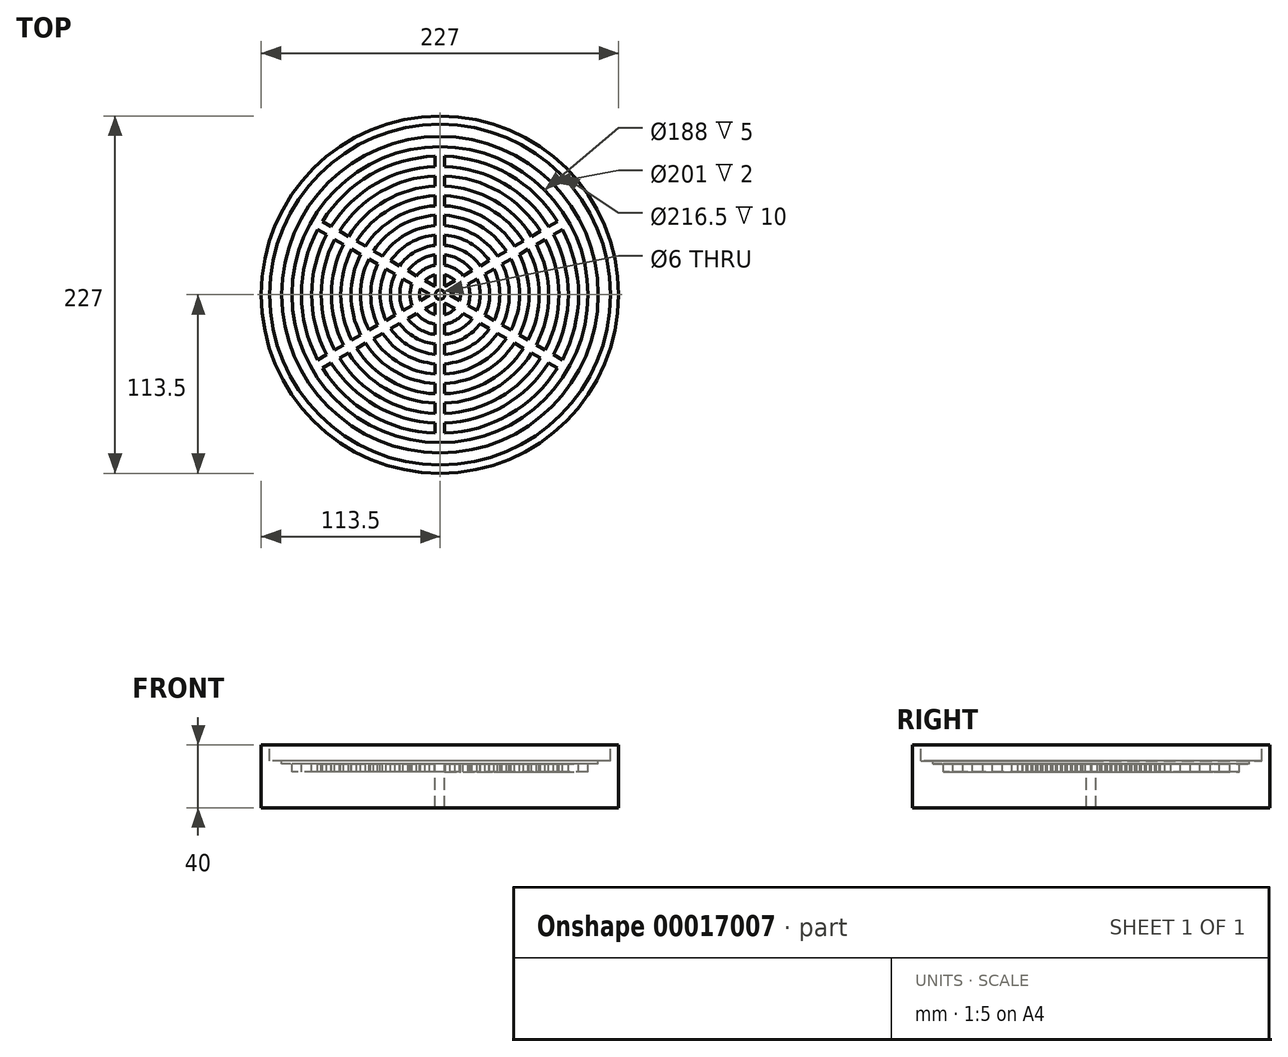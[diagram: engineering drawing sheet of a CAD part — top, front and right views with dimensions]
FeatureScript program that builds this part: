
annotation { "Feature Type Name" : "Feature", "Feature Type Description" : "" }
export const myFeature = defineFeature(function(context is Context, id is Id, definition is map)
    precondition{}
    {
        {
            var Q0;
            Q0=qCreatedBy(makeId("Front.planeOp"),FACE);
            var sketch = newSketch(context, id + "F0", { "sketchPlane" : qUnion([Q0])});
            skLineSegment(sketch, "E0", {"start": v(-113.5, 0) * mm, "end": v(-108.25, 0) * mm});
            skLineSegment(sketch, "E1", {"start": v(-108.25, 0) * mm, "end": v(-108.25, -10) * mm});
            skLineSegment(sketch, "E2", {"start": v(-108.25, -10) * mm, "end": v(-100.5, -10) * mm});
            skLineSegment(sketch, "E3", {"start": v(-100.5, -10) * mm, "end": v(-100.5, -12) * mm});
            skLineSegment(sketch, "E4", {"start": v(-3, -17) * mm, "end": v(-3, -40) * mm});
            skLineSegment(sketch, "E5", {"start": v(-3, -40) * mm, "end": v(-113.5, -40) * mm});
            skLineSegment(sketch, "E6", {"start": v(-113.5, -40) * mm, "end": v(-113.5, 0) * mm});
            skLineSegment(sketch, "E7", {"start": v(0, 37.77) * mm, "end": v(0, -35.64) * mm, "construction": true});
            skLineSegment(sketch, "E8", {"start": v(-100.5, -12) * mm, "end": v(-94, -12) * mm});
            skLineSegment(sketch, "E9", {"start": v(-94, -12) * mm, "end": v(-94, -17) * mm});
            skLineSegment(sketch, "E10", {"start": v(-94, -17) * mm, "end": v(-88, -17) * mm});
            skLineSegment(sketch, "E11", {"start": v(-88, -17) * mm, "end": v(-88, -12) * mm});
            skLineSegment(sketch, "E12.1.0.0", {"start": v(-75.5, -17) * mm, "end": v(-75.5, -12) * mm});
            skLineSegment(sketch, "E12.1.0.1", {"start": v(-81.5, -17) * mm, "end": v(-75.5, -17) * mm});
            skLineSegment(sketch, "E12.1.0.2", {"start": v(-81.5, -12) * mm, "end": v(-81.5, -17) * mm});
            skLineSegment(sketch, "E12.1.0.3", {"start": v(-88, -12) * mm, "end": v(-81.5, -12) * mm});
            skLineSegment(sketch, "E12.2.0.0", {"start": v(-63, -17) * mm, "end": v(-63, -12) * mm});
            skLineSegment(sketch, "E12.2.0.1", {"start": v(-69, -17) * mm, "end": v(-63, -17) * mm});
            skLineSegment(sketch, "E12.2.0.2", {"start": v(-69, -12) * mm, "end": v(-69, -17) * mm});
            skLineSegment(sketch, "E12.2.0.3", {"start": v(-75.5, -12) * mm, "end": v(-69, -12) * mm});
            skLineSegment(sketch, "E12.3.0.0", {"start": v(-50.5, -17) * mm, "end": v(-50.5, -12) * mm});
            skLineSegment(sketch, "E12.3.0.1", {"start": v(-56.5, -17) * mm, "end": v(-50.5, -17) * mm});
            skLineSegment(sketch, "E12.3.0.2", {"start": v(-56.5, -12) * mm, "end": v(-56.5, -17) * mm});
            skLineSegment(sketch, "E12.3.0.3", {"start": v(-63, -12) * mm, "end": v(-56.5, -12) * mm});
            skLineSegment(sketch, "E12.4.0.0", {"start": v(-38, -17) * mm, "end": v(-38, -12) * mm});
            skLineSegment(sketch, "E12.4.0.1", {"start": v(-44, -17) * mm, "end": v(-38, -17) * mm});
            skLineSegment(sketch, "E12.4.0.2", {"start": v(-44, -12) * mm, "end": v(-44, -17) * mm});
            skLineSegment(sketch, "E12.4.0.3", {"start": v(-50.5, -12) * mm, "end": v(-44, -12) * mm});
            skLineSegment(sketch, "E12.5.0.0", {"start": v(-25.5, -17) * mm, "end": v(-25.5, -12) * mm});
            skLineSegment(sketch, "E12.5.0.1", {"start": v(-31.5, -17) * mm, "end": v(-25.5, -17) * mm});
            skLineSegment(sketch, "E12.5.0.2", {"start": v(-31.5, -12) * mm, "end": v(-31.5, -17) * mm});
            skLineSegment(sketch, "E12.5.0.3", {"start": v(-38, -12) * mm, "end": v(-31.5, -12) * mm});
            skLineSegment(sketch, "E12.6.0.0", {"start": v(-13, -17) * mm, "end": v(-13, -12) * mm});
            skLineSegment(sketch, "E12.6.0.1", {"start": v(-19, -17) * mm, "end": v(-13, -17) * mm});
            skLineSegment(sketch, "E12.6.0.2", {"start": v(-19, -12) * mm, "end": v(-19, -17) * mm});
            skLineSegment(sketch, "E12.6.0.3", {"start": v(-25.5, -12) * mm, "end": v(-19, -12) * mm});
            skLineSegment(sketch, "E12.direction1", {"start": v(-88, -17) * mm, "end": v(-75.5, -17) * mm, "construction": true});
            skLineSegment(sketch, "E13.6.7.0", {"start": v(-6.5, -12) * mm, "end": v(-6.5, -17) * mm});
            skLineSegment(sketch, "E13.9.7.0", {"start": v(-13, -12) * mm, "end": v(-6.5, -12) * mm});
            skLineSegment(sketch, "E14", {"start": v(-6.5, -17) * mm, "end": v(-3, -17) * mm});
            skSolve(sketch);
        }
        {
            var Q0;
            Q0=makeQuery(id+"F0.imprint","IMPRINT",FACE,{"disambiguationData":[TD([[makeQuery(id+"F0.imprint","IMPRINT",EDGE,{"derivedFrom":sQuery(id+"F0.wireOp",EDGE,"E0")}),-1.0]])]});
            var Q1;
            Q1=sQuery(id+"F0.wireOp",EDGE,"E7");
            var Q2;
            Q2=sQuery(id+"F0.wireOp",EDGE,"E7");
            revolve(context, id + "F1", {"entities" : qUnion([Q0]), "surfaceEntities" : qUnion([Q1]), "axis" : qUnion([Q2]), "revolveType" : RevolveType.FULL});
        }
        {
            var Q0;
            Q0=qCreatedBy(makeId("Top.planeOp"),FACE);
            var sketch = newSketch(context, id + "F2", { "sketchPlane" : qUnion([Q0])});
            skLineSegment(sketch, "E15.rect.bottom", {"start": v(0, 94) * mm, "end": v(0, 94) * mm});
            skLineSegment(sketch, "E15.rect.top", {"start": v(0, -94) * mm, "end": v(0, -94) * mm});
            skLineSegment(sketch, "E15.rect.left", {"start": v(-3, 91) * mm, "end": v(-3, -91) * mm});
            skLineSegment(sketch, "E15.rect.right", {"start": v(3, 91) * mm, "end": v(3, -91) * mm});
            skPoint(sketch, "E15.rect.middle", {"position": v(0, 0) * mm});
            skPoint(sketch, "E16.visualSharp", {"position": v(-3, 94) * mm});
            skArc(sketch, "E16.filletArc", {"start": v(0, 94) * mm, "mid": v(-2.12, 93.12) * mm, "end": v(-3, 91) * mm});
            skPoint(sketch, "E17.visualSharp", {"position": v(3, 94) * mm});
            skArc(sketch, "E17.filletArc", {"start": v(3, 91) * mm, "mid": v(2.12, 93.12) * mm, "end": v(0, 94) * mm});
            skPoint(sketch, "E18.visualSharp", {"position": v(-3, -94) * mm});
            skArc(sketch, "E18.filletArc", {"start": v(-3, -91) * mm, "mid": v(-2.12, -93.12) * mm, "end": v(0, -94) * mm});
            skPoint(sketch, "E19.visualSharp", {"position": v(3, -94) * mm});
            skArc(sketch, "E19.filletArc", {"start": v(0, -94) * mm, "mid": v(2.12, -93.12) * mm, "end": v(3, -91) * mm});
            skArc(sketch, "E20.1.0", {"start": v(-81.4, -47) * mm, "mid": v(-79.58, -48.4) * mm, "end": v(-77.3, -48.1) * mm});
            skArc(sketch, "E20.1.1", {"start": v(-80.3, -42.9) * mm, "mid": v(-81.7, -44.72) * mm, "end": v(-81.4, -47) * mm});
            skLineSegment(sketch, "E20.1.2", {"start": v(-80.3, -42.9) * mm, "end": v(77.3, 48.1) * mm});
            skLineSegment(sketch, "E20.1.3", {"start": v(-77.3, -48.1) * mm, "end": v(80.3, 42.9) * mm});
            skArc(sketch, "E20.1.4", {"start": v(81.4, 47) * mm, "mid": v(79.58, 48.4) * mm, "end": v(77.3, 48.1) * mm});
            skArc(sketch, "E20.1.5", {"start": v(80.3, 42.9) * mm, "mid": v(81.7, 44.72) * mm, "end": v(81.4, 47) * mm});
            skArc(sketch, "E20.2.0", {"start": v(81.4, -47) * mm, "mid": v(81.7, -44.72) * mm, "end": v(80.3, -42.9) * mm});
            skArc(sketch, "E20.2.1", {"start": v(77.3, -48.1) * mm, "mid": v(79.58, -48.4) * mm, "end": v(81.4, -47) * mm});
            skLineSegment(sketch, "E20.2.2", {"start": v(77.3, -48.1) * mm, "end": v(-80.3, 42.9) * mm});
            skLineSegment(sketch, "E20.2.3", {"start": v(80.3, -42.9) * mm, "end": v(-77.3, 48.1) * mm});
            skArc(sketch, "E20.2.4", {"start": v(-81.4, 47) * mm, "mid": v(-81.7, 44.72) * mm, "end": v(-80.3, 42.9) * mm});
            skArc(sketch, "E20.2.5", {"start": v(-77.3, 48.1) * mm, "mid": v(-79.58, 48.4) * mm, "end": v(-81.4, 47) * mm});
            skSolve(sketch);
        }
        {
            var Q0;
            Q0 = qSketchRegion(id + "F2", true);
            var Q1;
            Q1=makeQuery(id+"F1.opRevolve","SWEPT_FACE",FACE,{"disambiguationData":[OSD([sQuery(id+"F0.wireOp",EDGE,"E12.1.0.1")])]});
            extrude(context, id + "F3", {"entities" : qUnion([Q0]), "operationType" : NewBodyOperationType.REMOVE, "endBound" : BoundingType.UP_TO_SURFACE, "oppositeDirection" : true, "endBoundEntityFace" : qUnion([Q1]), "depth" : 25 * mm});
        }
    });
